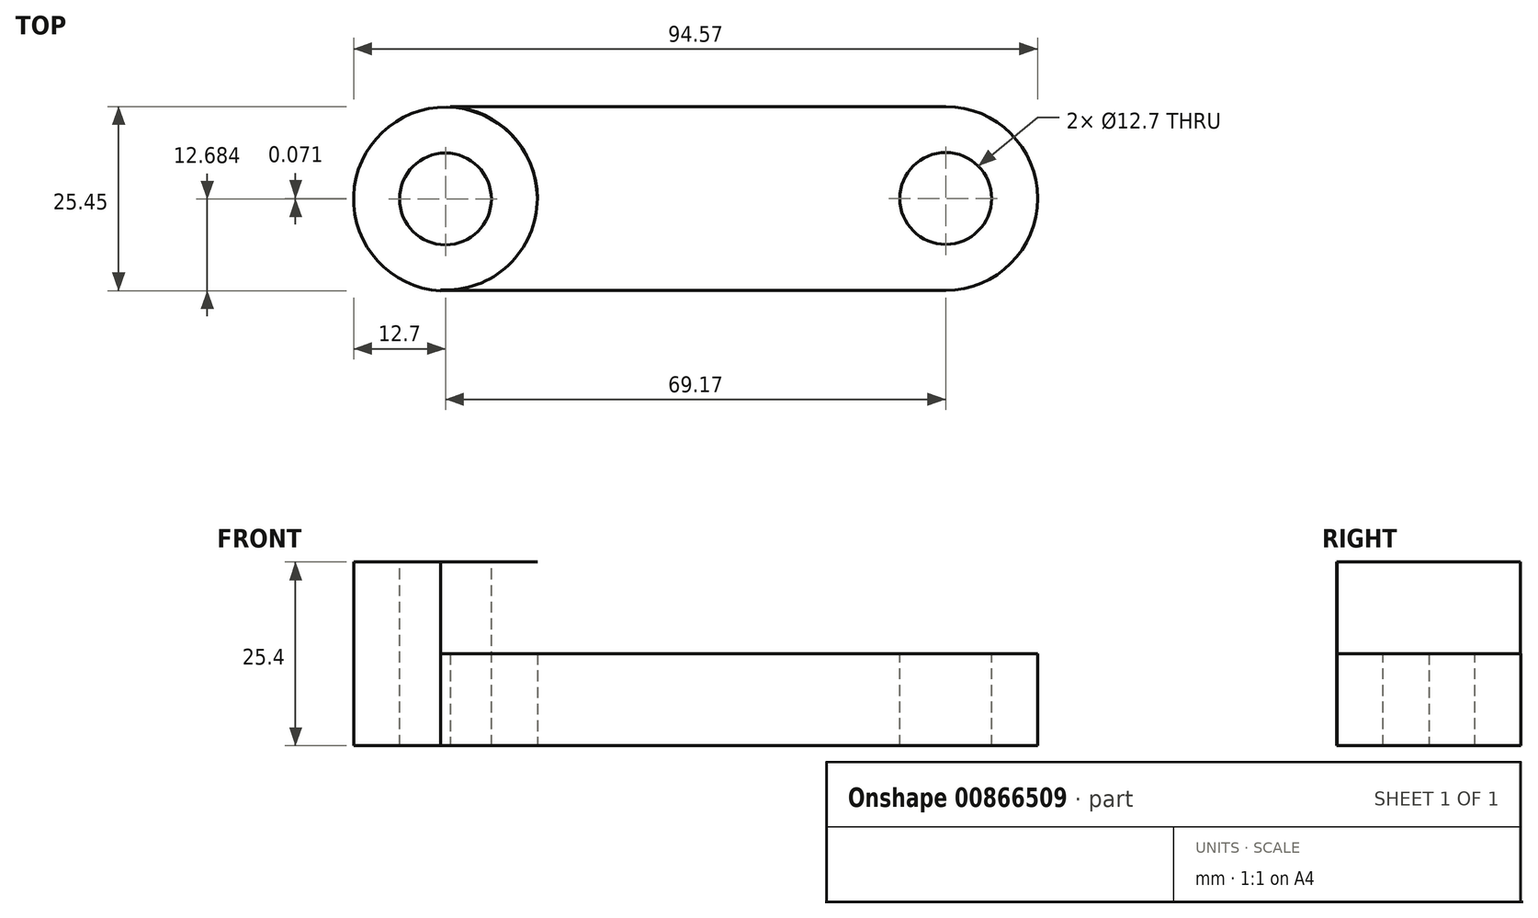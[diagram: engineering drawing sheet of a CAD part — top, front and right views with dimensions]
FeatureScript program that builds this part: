
annotation { "Feature Type Name" : "Feature", "Feature Type Description" : "" }
export const myFeature = defineFeature(function(context is Context, id is Id, definition is map)
    precondition{}
    {
        {
            var Q0;
            Q0=qCreatedBy(makeId("Top.planeOp"),FACE);
            var sketch = newSketch(context, id + "F0", { "sketchPlane" : qUnion([Q0])});
            skCircle(sketch, "E0", {"center": v(-99.19, 4.46) * mm, "radius": 12.7 * mm});
            skLineSegment(sketch, "E1.bottom", {"start": v(-99.87, 17.14) * mm, "end": v(-30.02, 17.14) * mm});
            skLineSegment(sketch, "E1.top", {"start": v(-99.87, -8.26) * mm, "end": v(-30.02, -8.26) * mm});
            skLineSegment(sketch, "E1.left", {"start": v(-99.87, 17.14) * mm, "end": v(-99.87, -8.26) * mm});
            skLineSegment(sketch, "E1.right", {"start": v(-30.02, 17.14) * mm, "end": v(-30.02, -8.26) * mm});
            skCircle(sketch, "E2", {"center": v(-30.02, 4.44) * mm, "radius": 12.7 * mm});
            skSolve(sketch);
        }
        {
            var Q0;
            {var subQ0=sQuery(id+"F0.wireOp",EDGE,"E1.top");Q0=makeQuery(id+"F0.imprint","IMPRINT",FACE,{"disambiguationData":[TD([[makeQuery(id+"F0.imprint","IMPRINT",EDGE,{"derivedFrom":subQ0}),1.0]])]});}
            var Q1;
            {var subQ0=sQuery(id+"F0.wireOp",EDGE,"E1.right");Q1=makeQuery(id+"F0.imprint","IMPRINT",FACE,{"disambiguationData":[TD([[makeQuery(id+"F0.imprint","IMPRINT",EDGE,{"derivedFrom":subQ0}),1.0]])]});}
            var Q2;
            {var subQ0=sQuery(id+"F0.wireOp",EDGE,"E1.right");Q2=makeQuery(id+"F0.imprint","IMPRINT",FACE,{"disambiguationData":[TD([[makeQuery(id+"F0.imprint","IMPRINT",EDGE,{"derivedFrom":subQ0}),-1.0]])]});}
            extrude(context, id + "F1", {"entities" : qUnion([Q0, Q1, Q2]), "depth" : 12.7 * mm, "offsetDistance" : 25.4 * mm});
        }
        {
            var Q0;
            Q0=makeQuery(id+"F1.opExtrude","CAP_FACE",FACE,{"disambiguationData":[OSD([sQuery(id+"F0.wireOp",EDGE,"E0"),sQuery(id+"F0.wireOp",EDGE,"E1.bottom"),sQuery(id+"F0.wireOp",EDGE,"E1.top"),sQuery(id+"F0.wireOp",EDGE,"E1.left"),sQuery(id+"F0.wireOp",EDGE,"E2")])],"isStart":true});
            var sketch = newSketch(context, id + "F2", { "sketchPlane" : qUnion([Q0])});
            skCircle(sketch, "E3", {"center": v(-99.19, -4.37) * mm, "radius": 12.7 * mm});
            skLineSegment(sketch, "E4.bottom", {"start": v(-99.87, 8.3) * mm, "end": v(-30.02, 8.3) * mm});
            skLineSegment(sketch, "E4.top", {"start": v(-99.87, -17.1) * mm, "end": v(-30.02, -17.1) * mm});
            skLineSegment(sketch, "E4.left", {"start": v(-99.87, 8.3) * mm, "end": v(-99.87, -17.1) * mm});
            skLineSegment(sketch, "E4.right", {"start": v(-30.02, 8.3) * mm, "end": v(-30.02, -17.1) * mm});
            skCircle(sketch, "E5", {"center": v(-30.02, -4.4) * mm, "radius": 12.7 * mm});
            skSolve(sketch);
        }
        {
            var Q0;
            {var subQ0=sQuery(id+"F2.wireOp",EDGE,"E4.left");var subQ1=sQuery(id+"F2.wireOp",EDGE,"E3");var subQ3=makeQuery(id+"F2.imprint","INTERSECT",VERTEX,{"derivedFrom":[subQ1,subQ0]});var subQ5=makeQuery(id+"F2.imprint","INTERSECT",VERTEX,{"derivedFrom":[makeQuery(id+"F1.opExtrude","CAP_EDGE",EDGE,{"disambiguationData":[OSD([sQuery(id+"F0.wireOp",EDGE,"E0")])],"isStart":true}),subQ0]});Q0=makeQuery(id+"F2.imprint","IMPRINT",FACE,{"disambiguationData":[TD([[makeQuery(id+"F2.imprint","IMPRINT",EDGE,{"disambiguationData":[TD([[subQ5,-1.0],[subQ3,1.0]])],"derivedFrom":subQ0}),-1.0]])]});}
            var Q1;
            {var subQ0=sQuery(id+"F2.wireOp",EDGE,"E4.left");var subQ1=sQuery(id+"F2.wireOp",EDGE,"E3");var subQ2=makeQuery(id+"F2.imprint","INTERSECT",VERTEX,{"derivedFrom":[subQ1,subQ0]});Q1=makeQuery(id+"F2.imprint","IMPRINT",FACE,{"disambiguationData":[TD([[makeQuery(id+"F2.imprint","IMPRINT",EDGE,{"disambiguationData":[TD([[subQ2,-1.0]])],"derivedFrom":subQ1}),1.0]])]});}
            var Q2;
            Q2=sQuery(id+"F2.wireOp",EDGE,"E3");
            extrude(context, id + "F3", {"entities" : qUnion([Q0, Q1]), "operationType" : NewBodyOperationType.ADD, "surfaceEntities" : qUnion([Q2]), "oppositeDirection" : true, "depth" : 25.4 * mm, "offsetDistance" : 25.4 * mm});
        }
        {
            var Q0;
            Q0=makeQuery(id+"F3.opExtrude","CAP_FACE",FACE,{"disambiguationData":[OSD([sQuery(id+"F0.wireOp",EDGE,"E0"),sQuery(id+"F2.wireOp",EDGE,"E3"),sQuery(id+"F2.wireOp",EDGE,"E4.left")])],"isStart":false});
            var sketch = newSketch(context, id + "F4", { "sketchPlane" : qUnion([Q0])});
            skCircle(sketch, "E6", {"center": v(-99.19, 4.37) * mm, "radius": 6.35 * mm});
            skSolve(sketch);
        }
        {
            var Q0;
            Q0=makeQuery(id+"F4.imprint","IMPRINT",FACE,{"disambiguationData":[TD([[makeQuery(id+"F4.imprint","IMPRINT",EDGE,{"derivedFrom":sQuery(id+"F4.wireOp",EDGE,"E6")}),1.0]])]});
            var Q1;
            Q1=sQuery(id+"F4.wireOp",EDGE,"E6");
            extrude(context, id + "F5", {"entities" : qUnion([Q0]), "operationType" : NewBodyOperationType.REMOVE, "surfaceEntities" : qUnion([Q1]), "oppositeDirection" : true, "depth" : 25.4 * mm, "offsetDistance" : 25.4 * mm});
        }
        {
            var Q0;
            Q0=makeQuery(id+"F1.opExtrude","CAP_FACE",FACE,{"disambiguationData":[OSD([sQuery(id+"F0.wireOp",EDGE,"E0"),sQuery(id+"F0.wireOp",EDGE,"E1.bottom"),sQuery(id+"F0.wireOp",EDGE,"E1.top"),sQuery(id+"F0.wireOp",EDGE,"E1.left"),sQuery(id+"F0.wireOp",EDGE,"E2")])],"isStart":false});
            var sketch = newSketch(context, id + "F6", { "sketchPlane" : qUnion([Q0])});
            skCircle(sketch, "E7", {"center": v(-30.02, 4.44) * mm, "radius": 6.35 * mm});
            skSolve(sketch);
        }
        {
            var Q0;
            Q0 = qSketchRegion(id + "F6", true);
            extrude(context, id + "F7", {"entities" : qUnion([Q0]), "operationType" : NewBodyOperationType.REMOVE, "oppositeDirection" : true, "depth" : 12.7 * mm, "offsetDistance" : 25.4 * mm});
        }
    });
